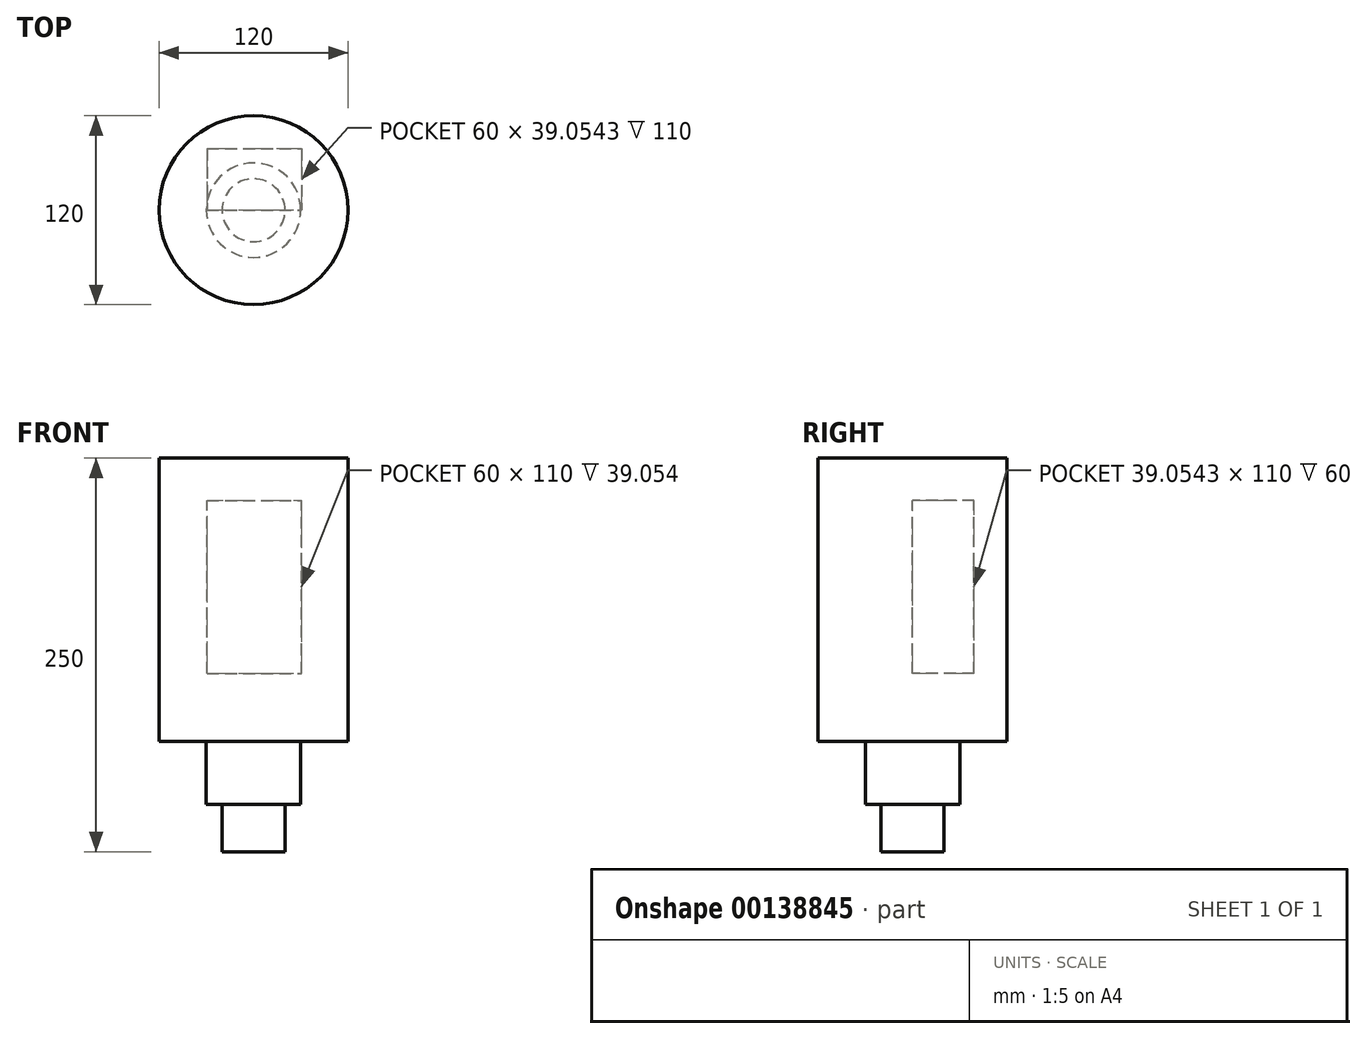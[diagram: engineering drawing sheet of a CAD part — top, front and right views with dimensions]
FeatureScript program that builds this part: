
annotation { "Feature Type Name" : "Feature", "Feature Type Description" : "" }
export const myFeature = defineFeature(function(context is Context, id is Id, definition is map)
    precondition{}
    {
        {
            var Q0;
            Q0=qCreatedBy(makeId("Top.planeOp"),FACE);
            var sketch = newSketch(context, id + "F0", { "sketchPlane" : qUnion([Q0])});
            skCircle(sketch, "E0", {"center": v(0, 0) * mm, "radius": 20 * mm});
            skSolve(sketch);
        }
        {
            var Q0;
            Q0=makeQuery(id+"F0.imprint","IMPRINT",FACE,{"disambiguationData":[TD([[makeQuery(id+"F0.imprint","IMPRINT",EDGE,{"derivedFrom":sQuery(id+"F0.wireOp",EDGE,"E0")}),1.0]])]});
            extrude(context, id + "F1", {"entities" : qUnion([Q0]), "oppositeDirection" : true, "depth" : 30 * mm});
        }
        {
            var Q0;
            Q0=qCreatedBy(makeId("Top.planeOp"),FACE);
            var sketch = newSketch(context, id + "F2", { "sketchPlane" : qUnion([Q0])});
            skCircle(sketch, "E1", {"center": v(0, 0) * mm, "radius": 30 * mm});
            skSolve(sketch);
        }
        {
            var Q0;
            Q0=makeQuery(id+"F2.imprint","IMPRINT",FACE,{"disambiguationData":[TD([[makeQuery(id+"F2.imprint","IMPRINT",EDGE,{"derivedFrom":sQuery(id+"F2.wireOp",EDGE,"E1")}),1.0]])]});
            extrude(context, id + "F3", {"entities" : qUnion([Q0]), "operationType" : NewBodyOperationType.ADD, "depth" : 40 * mm});
        }
        {
            var Q0;
            Q0=makeQuery(id+"F3.opExtrude","CAP_FACE",FACE,{"disambiguationData":[OSD([sQuery(id+"F2.wireOp",EDGE,"E1")])],"isStart":false});
            var sketch = newSketch(context, id + "F4", { "sketchPlane" : qUnion([Q0])});
            skCircle(sketch, "E2", {"center": v(0, 0) * mm, "radius": 60 * mm});
            skSolve(sketch);
        }
        {
            var Q0;
            Q0 = qSketchRegion(id + "F4", true);
            extrude(context, id + "F5", {"entities" : qUnion([Q0]), "operationType" : NewBodyOperationType.ADD, "depth" : 180 * mm});
        }
        {
            var Q0;
            Q0=qCreatedBy(makeId("Front.planeOp"),FACE);
            var sketch = newSketch(context, id + "F6", { "sketchPlane" : qUnion([Q0])});
            skLineSegment(sketch, "E3", {"start": v(-29.59, 83.22) * mm, "end": v(30.41, 83.22) * mm});
            skLineSegment(sketch, "E4", {"start": v(0, 218.42) * mm, "end": v(0, 41.17) * mm, "construction": true});
            skLineSegment(sketch, "E5", {"start": v(-29.59, 83.22) * mm, "end": v(-29.59, 193.22) * mm});
            skLineSegment(sketch, "E6", {"start": v(30.41, 83.22) * mm, "end": v(30.41, 193.22) * mm});
            skLineSegment(sketch, "E7", {"start": v(-29.59, 193.22) * mm, "end": v(30.41, 193.22) * mm});
            skSolve(sketch);
        }
        {
            var Q0;
            Q0=makeQuery(id+"F6.imprint","IMPRINT",FACE,{"disambiguationData":[TD([[makeQuery(id+"F6.imprint","IMPRINT",EDGE,{"derivedFrom":sQuery(id+"F6.wireOp",EDGE,"E3")}),1.0]])]});
            extrude(context, id + "F7", {"entities" : qUnion([Q0]), "operationType" : NewBodyOperationType.REMOVE, "oppositeDirection" : true, "depth" : 39.05 * mm});
        }
    });
